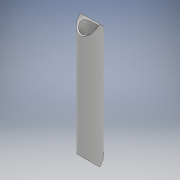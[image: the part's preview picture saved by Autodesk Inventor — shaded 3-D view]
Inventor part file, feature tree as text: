
AUTODESK INVENTOR PART (.ipt)
format: ipt  version: 2018 (Build 220112000, 112)  size: 118,272 bytes
history: native  units: mm
features: sketch x4, extrude x3, other x2, hole x1
ambient origin geometry x8: Origin, YZ Plane, XZ Plane, XY Plane, X Axis, Y Axis, Z Axis, Center Point
bodies: Body1 (feature_tree)
feature tree (10):
  other  "ソリッド1"
  extrude  "押し出し1"  Depth=27.2mm
  hole  "穴1"  [1 undecoded]
  other  "作業平面1"
  extrude  "押し出し3"  TaperAngle=0.0deg  [1 undecoded]
  extrude  "押し出し4"  Depth=27.2mm TaperAngle=0.0deg
  sketch  "スケッチ1"
  sketch  "スケッチ3"
  sketch  "スケッチ4"
  sketch  "スケッチ5"
note: 2 required parameter values undecoded (feature->parameter linkage not recoverable at this tier; creation-order binding heuristic only, values carry confidence <= 0.55)
